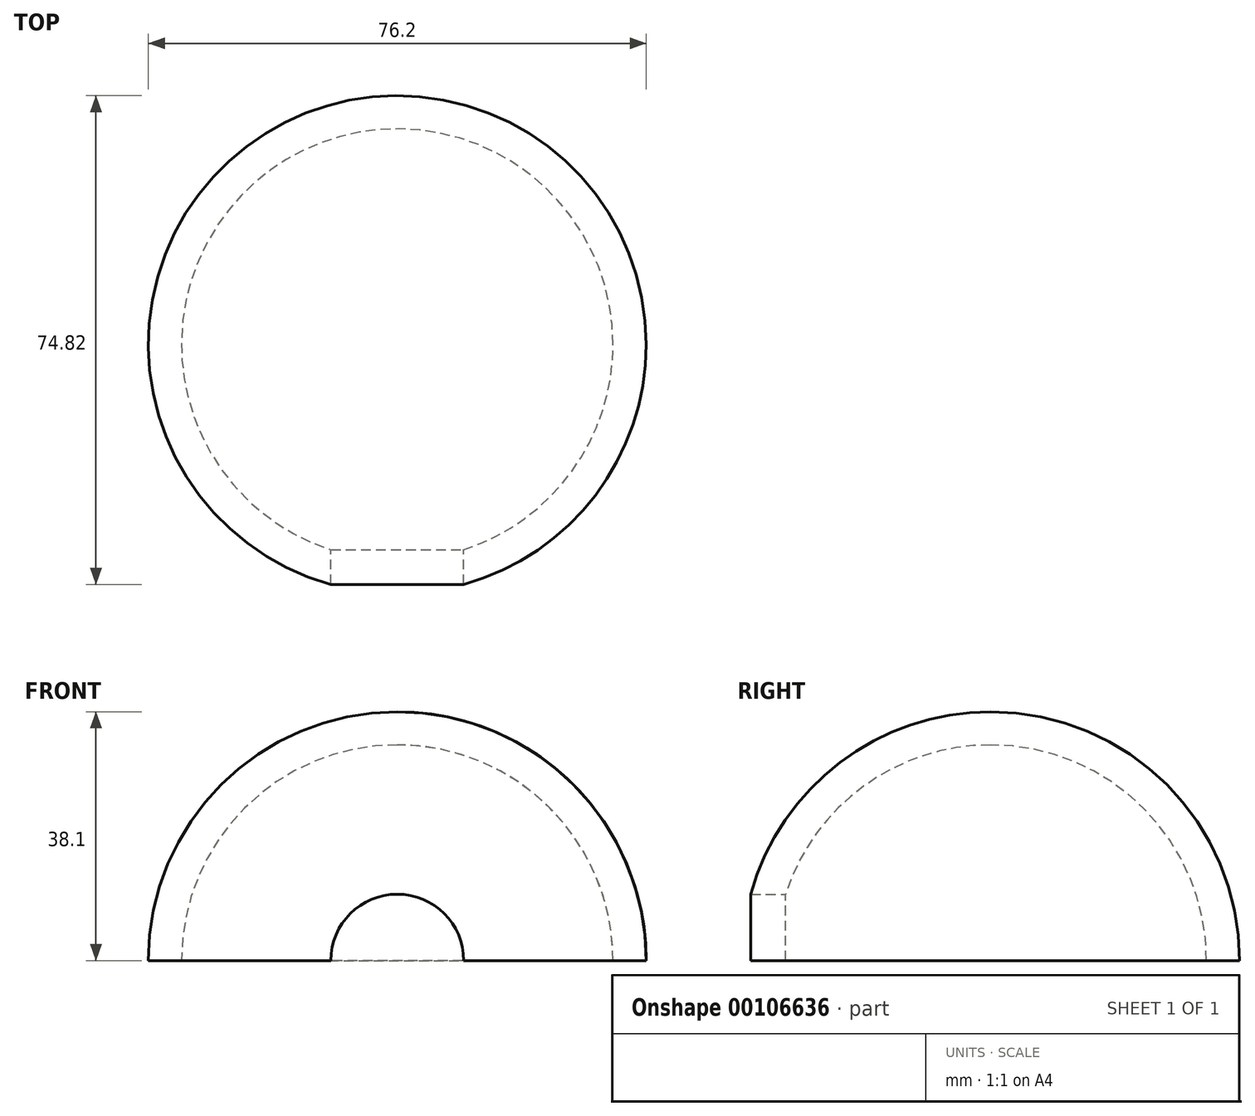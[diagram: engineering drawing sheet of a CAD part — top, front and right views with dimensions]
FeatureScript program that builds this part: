
annotation { "Feature Type Name" : "Feature", "Feature Type Description" : "" }
export const myFeature = defineFeature(function(context is Context, id is Id, definition is map)
    precondition{}
    {
        {
            var Q0;
            Q0=qCreatedBy(makeId("Front.planeOp"),FACE);
            var sketch = newSketch(context, id + "F0", { "sketchPlane" : qUnion([Q0])});
            skLineSegment(sketch, "E0", {"start": v(0, 0) * mm, "end": v(0, 38.1) * mm});
            skLineSegment(sketch, "E1", {"start": v(0, 0) * mm, "end": v(38.1, 0) * mm});
            skArc(sketch, "E2", {"start": v(38.1, 0) * mm, "mid": v(26.94, 26.94) * mm, "end": v(0, 38.1) * mm});
            skSolve(sketch);
        }
        {
            var Q0;
            Q0=makeQuery(id+"F0.imprint","IMPRINT",FACE,{"disambiguationData":[TD([[makeQuery(id+"F0.imprint","IMPRINT",EDGE,{"derivedFrom":sQuery(id+"F0.wireOp",EDGE,"E0")}),-1.0]])]});
            var Q1;
            Q1=sQuery(id+"F0.wireOp",EDGE,"E0");
            revolve(context, id + "F1", {"entities" : qUnion([Q0]), "axis" : qUnion([Q1]), "revolveType" : RevolveType.FULL});
        }
        {
            var Q0;
            Q0=qCreatedBy(makeId("Front.planeOp"),FACE);
            var sketch = newSketch(context, id + "F2", { "sketchPlane" : qUnion([Q0])});
            skLineSegment(sketch, "E3", {"start": v(0, 0) * mm, "end": v(-33.02, 0) * mm});
            skLineSegment(sketch, "E4", {"start": v(0, 0) * mm, "end": v(0, 33.02) * mm});
            skArc(sketch, "E5", {"start": v(0, 33.02) * mm, "mid": v(-23.35, 23.35) * mm, "end": v(-33.02, 0) * mm});
            skSolve(sketch);
        }
        {
            var Q0;
            Q0 = qSketchRegion(id + "F2", true);
            var Q1;
            Q1=sQuery(id+"F2.wireOp",EDGE,"E4");
            revolve(context, id + "F3", {"operationType" : NewBodyOperationType.REMOVE, "entities" : qUnion([Q0]), "axis" : qUnion([Q1]), "revolveType" : RevolveType.FULL, "oppositeDirection" : true});
        }
        {
            var Q0;
            Q0=qCreatedBy(makeId("Front.planeOp"),FACE);
            var sketch = newSketch(context, id + "F4", { "sketchPlane" : qUnion([Q0])});
            skArc(sketch, "E6", {"start": v(10.16, 0) * mm, "mid": v(0, 10.16) * mm, "end": v(-10.16, 0) * mm});
            skLineSegment(sketch, "E7", {"start": v(-10.16, 0) * mm, "end": v(0, 0) * mm});
            skLineSegment(sketch, "E8", {"start": v(10.16, 0) * mm, "end": v(0, 0) * mm});
            skSolve(sketch);
        }
        {
            var Q0;
            Q0 = qSketchRegion(id + "F4", true);
            extrude(context, id + "F5", {"entities" : qUnion([Q0]), "operationType" : NewBodyOperationType.REMOVE, "depth" : 38.1 * mm});
        }
    });
